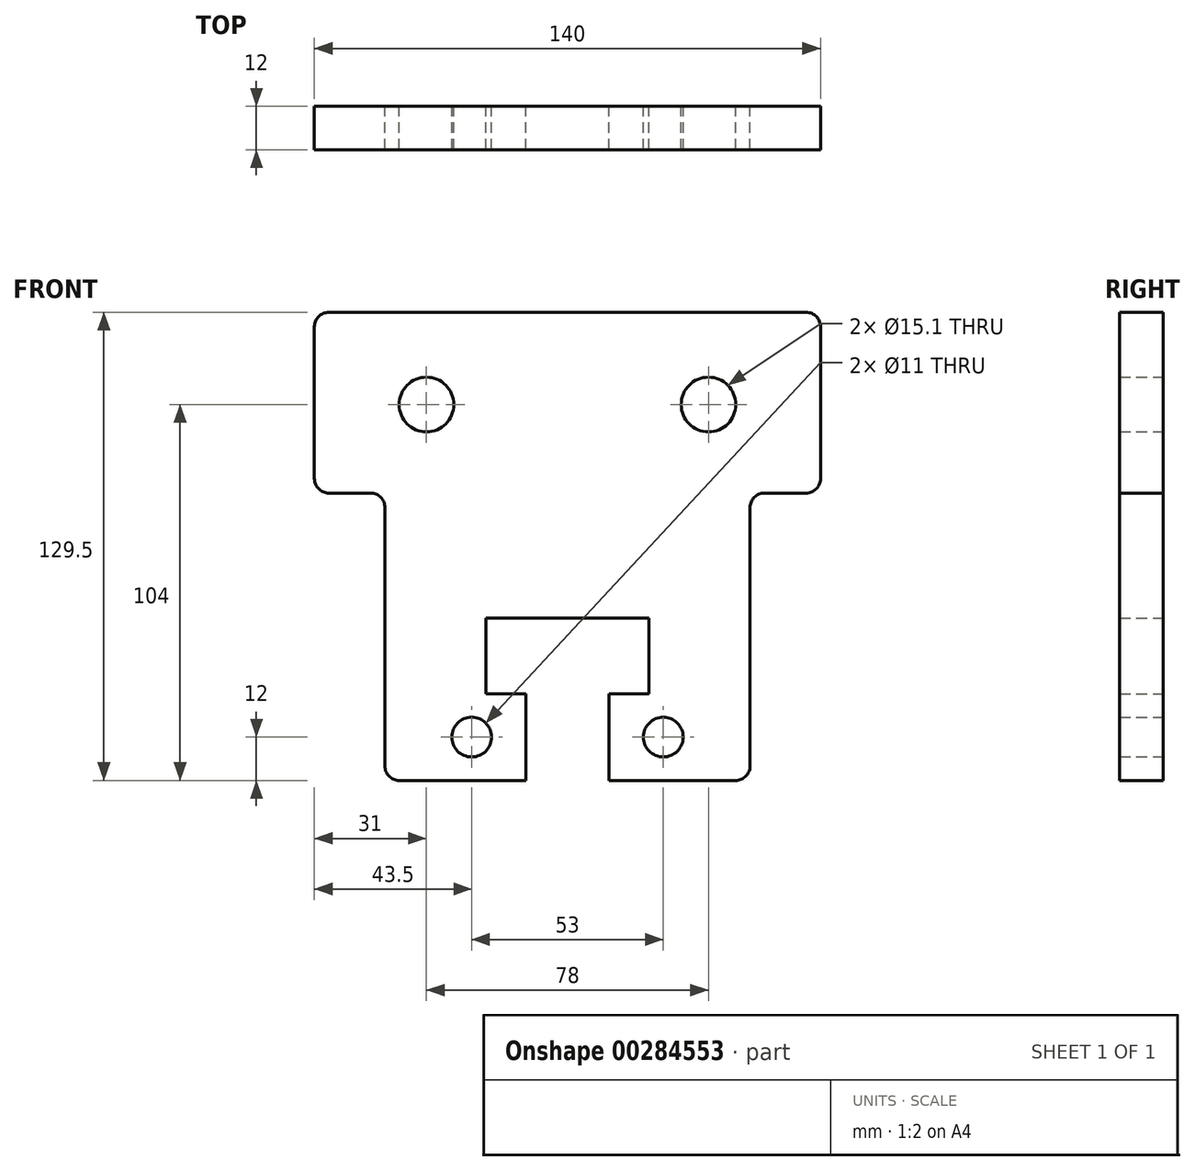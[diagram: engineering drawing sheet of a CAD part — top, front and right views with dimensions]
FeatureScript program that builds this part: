
annotation { "Feature Type Name" : "Feature", "Feature Type Description" : "" }
export const myFeature = defineFeature(function(context is Context, id is Id, definition is map)
    precondition{}
    {
        {
            var Q0;
            Q0=qCreatedBy(makeId("Front.planeOp"),FACE);
            var sketch = newSketch(context, id + "F0", { "sketchPlane" : qUnion([Q0])});
            skLineSegment(sketch, "E0", {"start": v(0, 0) * mm, "end": v(-70, 0) * mm});
            skLineSegment(sketch, "E1", {"start": v(-70, 0) * mm, "end": v(-70, -50) * mm});
            skLineSegment(sketch, "E2", {"start": v(-70, -50) * mm, "end": v(-50.5, -50) * mm});
            skLineSegment(sketch, "E3", {"start": v(-50.5, -50) * mm, "end": v(-50.5, -129.5) * mm});
            skLineSegment(sketch, "E4", {"start": v(-50.5, -129.5) * mm, "end": v(-11.5, -129.5) * mm});
            skLineSegment(sketch, "E5", {"start": v(-11.5, -129.5) * mm, "end": v(-11.5, -105.5) * mm});
            skLineSegment(sketch, "E6", {"start": v(-11.5, -105.5) * mm, "end": v(-22.5, -105.5) * mm});
            skLineSegment(sketch, "E7", {"start": v(-22.5, -105.5) * mm, "end": v(-22.5, -84.6) * mm});
            skLineSegment(sketch, "E8", {"start": v(-22.5, -84.6) * mm, "end": v(0, -84.6) * mm});
            skLineSegment(sketch, "E9", {"start": v(0, -84.6) * mm, "end": v(0, 0) * mm});
            skCircle(sketch, "E10", {"center": v(-39, -25.5) * mm, "radius": 7.55 * mm});
            skCircle(sketch, "E11", {"center": v(-26.5, -117.5) * mm, "radius": 5.5 * mm});
            skSolve(sketch);
        }
        {
            var Q0;
            Q0=makeQuery(id+"F0.imprint","IMPRINT",FACE,{"disambiguationData":[TD([[makeQuery(id+"F0.imprint","IMPRINT",EDGE,{"derivedFrom":sQuery(id+"F0.wireOp",EDGE,"E0")}),1.0]])]});
            extrude(context, id + "F1", {"entities" : qUnion([Q0]), "depth" : 12 * mm});
        }
        {
            var Q0;
            Q0=makeQuery(id+"F1.opExtrude","SWEPT_EDGE",EDGE,{"disambiguationData":[OSD([sQuery(id+"F0.wireOp",EDGE,"E3"),sQuery(id+"F0.wireOp",EDGE,"E4")])]});
            var Q1;
            Q1=makeQuery(id+"F1.opExtrude","SWEPT_EDGE",EDGE,{"disambiguationData":[OSD([sQuery(id+"F0.wireOp",EDGE,"E2"),sQuery(id+"F0.wireOp",EDGE,"E3")])]});
            var Q2;
            Q2=makeQuery(id+"F1.opExtrude","SWEPT_EDGE",EDGE,{"disambiguationData":[OSD([sQuery(id+"F0.wireOp",EDGE,"E1"),sQuery(id+"F0.wireOp",EDGE,"E2")])]});
            var Q3;
            Q3=makeQuery(id+"F1.opExtrude","SWEPT_EDGE",EDGE,{"disambiguationData":[OSD([sQuery(id+"F0.wireOp",EDGE,"E0"),sQuery(id+"F0.wireOp",EDGE,"E1")])]});
            fillet(context, id + "F2", {"entities" : qUnion([Q0, Q1, Q2, Q3]), "radius" : 4 * mm, "tangentPropagation" : true, "allowEdgeOverflow" : false});
        }
        {
            var Q0;
            Q0=makeQuery(id+"F1.opExtrude","SWEPT_BODY",BODY,{"disambiguationData":[OSD([sQuery(id+"F0.wireOp",EDGE,"E0"),sQuery(id+"F0.wireOp",EDGE,"E1"),sQuery(id+"F0.wireOp",EDGE,"E2"),sQuery(id+"F0.wireOp",EDGE,"E3"),sQuery(id+"F0.wireOp",EDGE,"E4"),sQuery(id+"F0.wireOp",EDGE,"E5"),sQuery(id+"F0.wireOp",EDGE,"E6"),sQuery(id+"F0.wireOp",EDGE,"E7"),sQuery(id+"F0.wireOp",EDGE,"E8"),sQuery(id+"F0.wireOp",EDGE,"E9"),sQuery(id+"F0.wireOp",EDGE,"E10"),sQuery(id+"F0.wireOp",EDGE,"E11")])]});
            var Q1;
            Q1=makeQuery(id+"F1.opExtrude","SWEPT_FACE",FACE,{"disambiguationData":[OSD([sQuery(id+"F0.wireOp",EDGE,"E9")])]});
            mirror(context, id + "F3", {"operationType" : NewBodyOperationType.ADD, "entities" : qUnion([Q0]), "mirrorPlane" : qUnion([Q1])});
        }
    });
